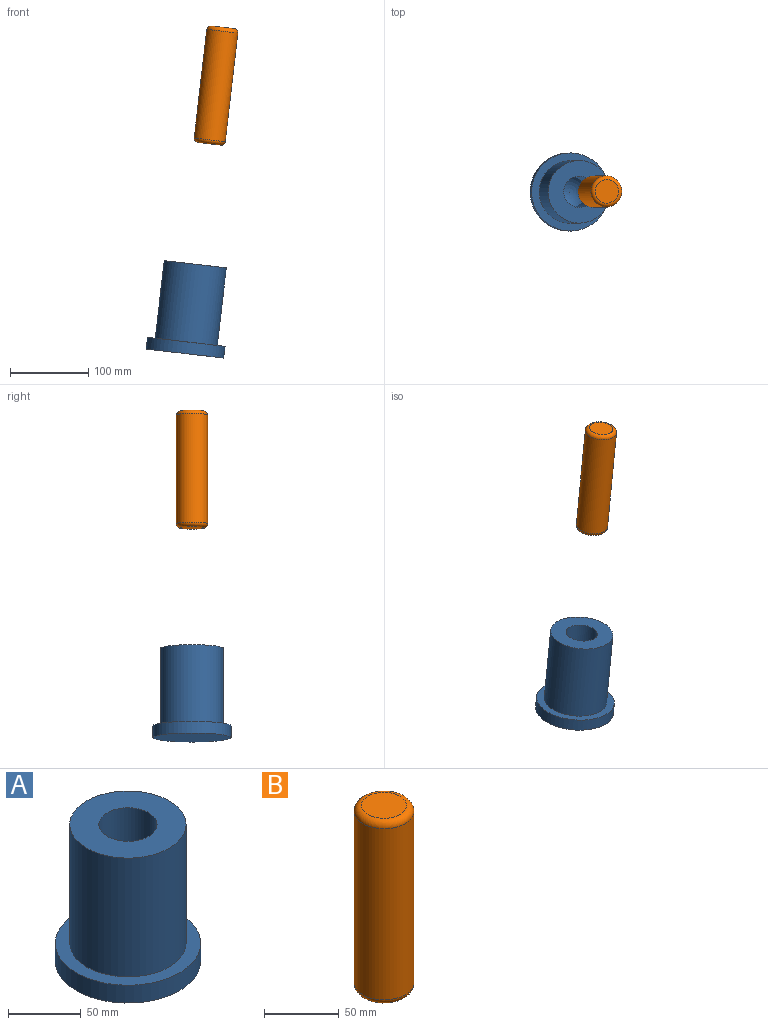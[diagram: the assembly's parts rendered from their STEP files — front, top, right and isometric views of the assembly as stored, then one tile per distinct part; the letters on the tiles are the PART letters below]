
ASSEMBLY  parts=2 mates=1
PART A: 7 faces, bbox 100x100x115 mm
  f0: sphere r=26.72mm, area 1511.1mm2, adj f1
  f1: cylinder r=20mm len=100mm, axis (0,0,-1), area 12566.4mm2, adj f0,f2
  f2: plane 80x80mm, normal (0,0,1), area 3769.9mm2, adj f1,f3
  f3: cylinder r=40mm len=100mm, axis (0,0,-1), area 25132.7mm2, adj f2,f4
  f4: plane 100x100mm, normal (0,0,1), area 2827.4mm2, adj f3,f5
  f5: cylinder r=50mm len=100mm, axis (0,0,-1), area 4712.4mm2, adj f4,f6
  f6: plane 100x100mm, normal (0,0,-1), area 7854mm2, adj f5
PART B: 5 faces, bbox 43.3x43.3x150 mm
  f0: plane 30x30mm, normal (0,0,1), area 706.9mm2, adj f3
  f1: cylinder r=20mm len=140mm, axis (0,0,1), area 17592.9mm2, adj f3,f4
  f2: plane 30x30mm, normal (0,0,-1), area 706.9mm2, adj f4
  f3: torus R=15mm, axis (0,0,-1), area 897.3mm2, adj f0,f1
  f4: torus R=15mm, axis (0,0,-1), area 897.3mm2, adj f1,f2
PLACE A rot(axis=(0,1,0),6.6deg) t=(-13.89,-35.78,12.01)mm
PLACE B rot(axis=(0,-1,0),173.4deg) t=(46.7,-35.78,415.25)mm
MATE cylindrical B.f1 <-> A.f1  axis (-0.12,0,-0.99) through (36.4,-35.78,411.41)mm
